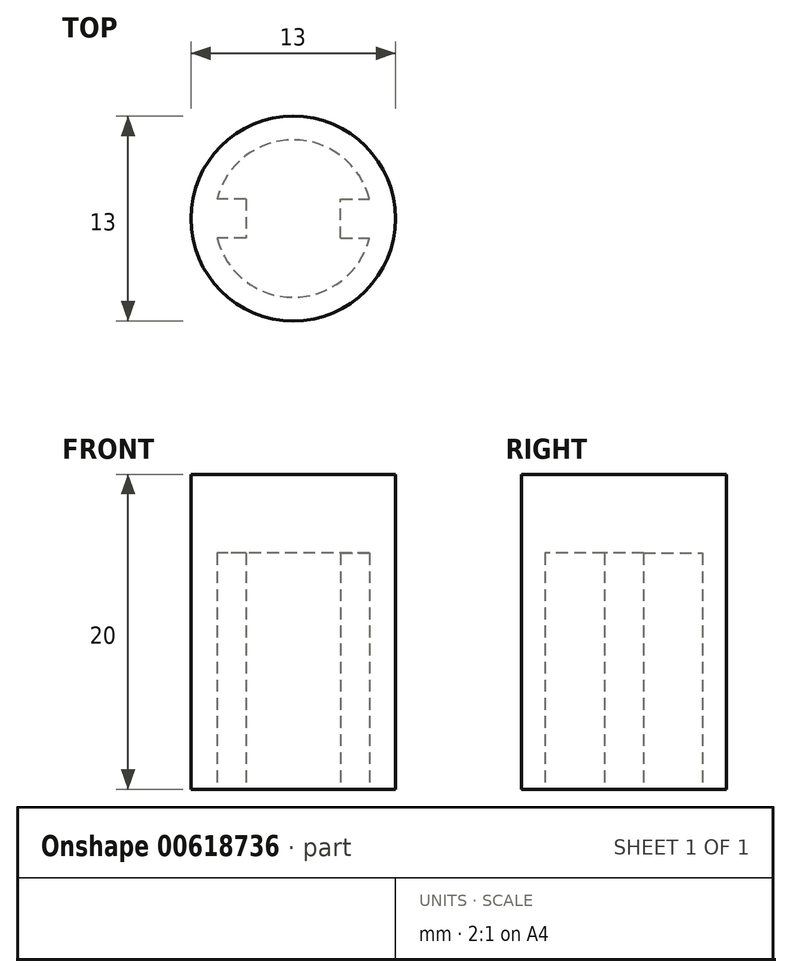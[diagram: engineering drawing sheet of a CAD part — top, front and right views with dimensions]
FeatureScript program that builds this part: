
annotation { "Feature Type Name" : "Feature", "Feature Type Description" : "" }
export const myFeature = defineFeature(function(context is Context, id is Id, definition is map)
    precondition{}
    {
        {
            var Q0;
            Q0=qCreatedBy(makeId("Top.planeOp"),FACE);
            var sketch = newSketch(context, id + "F0", { "sketchPlane" : qUnion([Q0])});
            skLineSegment(sketch, "E0", {"start": v(3, 1.25) * mm, "end": v(3, 0) * mm});
            skLineSegment(sketch, "E1.MirrorCS", {"start": v(3, -1.25) * mm, "end": v(3, 0) * mm});
            skLineSegment(sketch, "E2", {"start": v(3, 1.25) * mm, "end": v(4.84, 1.25) * mm});
            skLineSegment(sketch, "E3", {"start": v(3, -1.25) * mm, "end": v(4.84, -1.25) * mm});
            skLineSegment(sketch, "E4.MirrorCS", {"start": v(-3, 1.25) * mm, "end": v(-4.84, 1.25) * mm});
            skLineSegment(sketch, "E5.MirrorCS", {"start": v(-3, -1.25) * mm, "end": v(-4.84, -1.25) * mm});
            skLineSegment(sketch, "E6.MirrorCS", {"start": v(-3, 1.25) * mm, "end": v(-3, 0) * mm});
            skLineSegment(sketch, "E7.MirrorCS", {"start": v(-3, -1.25) * mm, "end": v(-3, 0) * mm});
            skArc(sketch, "E8", {"start": v(-4.84, 1.25) * mm, "mid": v(0, 5) * mm, "end": v(4.84, 1.25) * mm});
            skArc(sketch, "E9", {"start": v(4.84, -1.25) * mm, "mid": v(0, -5) * mm, "end": v(-4.84, -1.25) * mm});
            skSolve(sketch);
        }
        {
            var Q0;
            Q0=qCreatedBy(makeId("Top.planeOp"),FACE);
            var sketch = newSketch(context, id + "F1", { "sketchPlane" : qUnion([Q0])});
            skCircle(sketch, "E10", {"center": v(0, 0) * mm, "radius": 6.5 * mm});
            skSolve(sketch);
        }
        {
            var Q0;
            Q0 = qSketchRegion(id + "F1", true);
            extrude(context, id + "F2", {"entities" : qUnion([Q0]), "depth" : 20 * mm, "offsetDistance" : 25 * mm});
        }
        {
            var Q0;
            Q0=makeQuery(id+"F0.imprint","IMPRINT",FACE,{"disambiguationData":[TD([[makeQuery(id+"F0.imprint","IMPRINT",EDGE,{"derivedFrom":sQuery(id+"F0.wireOp",EDGE,"E0")}),-1.0]])]});
            extrude(context, id + "F3", {"entities" : qUnion([Q0]), "operationType" : NewBodyOperationType.REMOVE, "depth" : 15 * mm, "offsetDistance" : 25 * mm});
        }
    });
